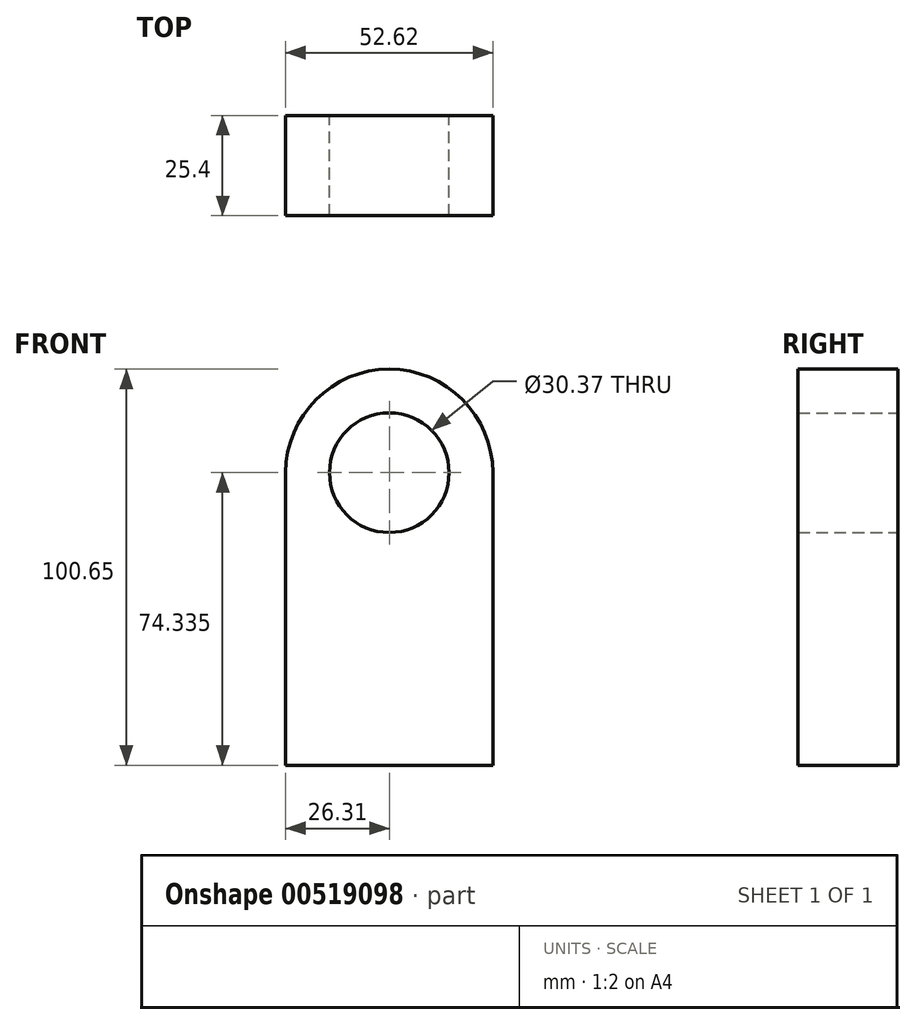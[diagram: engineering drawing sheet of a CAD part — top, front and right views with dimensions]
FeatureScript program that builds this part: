
annotation { "Feature Type Name" : "Feature", "Feature Type Description" : "" }
export const myFeature = defineFeature(function(context is Context, id is Id, definition is map)
    precondition{}
    {
        {
            var Q0;
            Q0=qCreatedBy(makeId("Front.planeOp"),FACE);
            var sketch = newSketch(context, id + "F0", { "sketchPlane" : qUnion([Q0])});
            skLineSegment(sketch, "E0.top", {"start": v(26.31, -37.17) * mm, "end": v(-26.31, -37.17) * mm});
            skLineSegment(sketch, "E0.left", {"start": v(26.31, 37.17) * mm, "end": v(26.31, -37.17) * mm});
            skLineSegment(sketch, "E0.right", {"start": v(-26.31, 37.17) * mm, "end": v(-26.31, -37.17) * mm});
            skPoint(sketch, "E0.middle", {"position": v(0, 0) * mm});
            skArc(sketch, "E1", {"start": v(26.31, 37.17) * mm, "mid": v(0, 63.48) * mm, "end": v(-26.31, 37.17) * mm});
            skCircle(sketch, "E2", {"center": v(0, 37.17) * mm, "radius": 15.19 * mm});
            skSolve(sketch);
        }
        {
            var Q0;
            Q0 = qSketchRegion(id + "F0", true);
            extrude(context, id + "F1", {"entities" : qUnion([Q0]), "depth" : 25.4 * mm});
        }
    });
